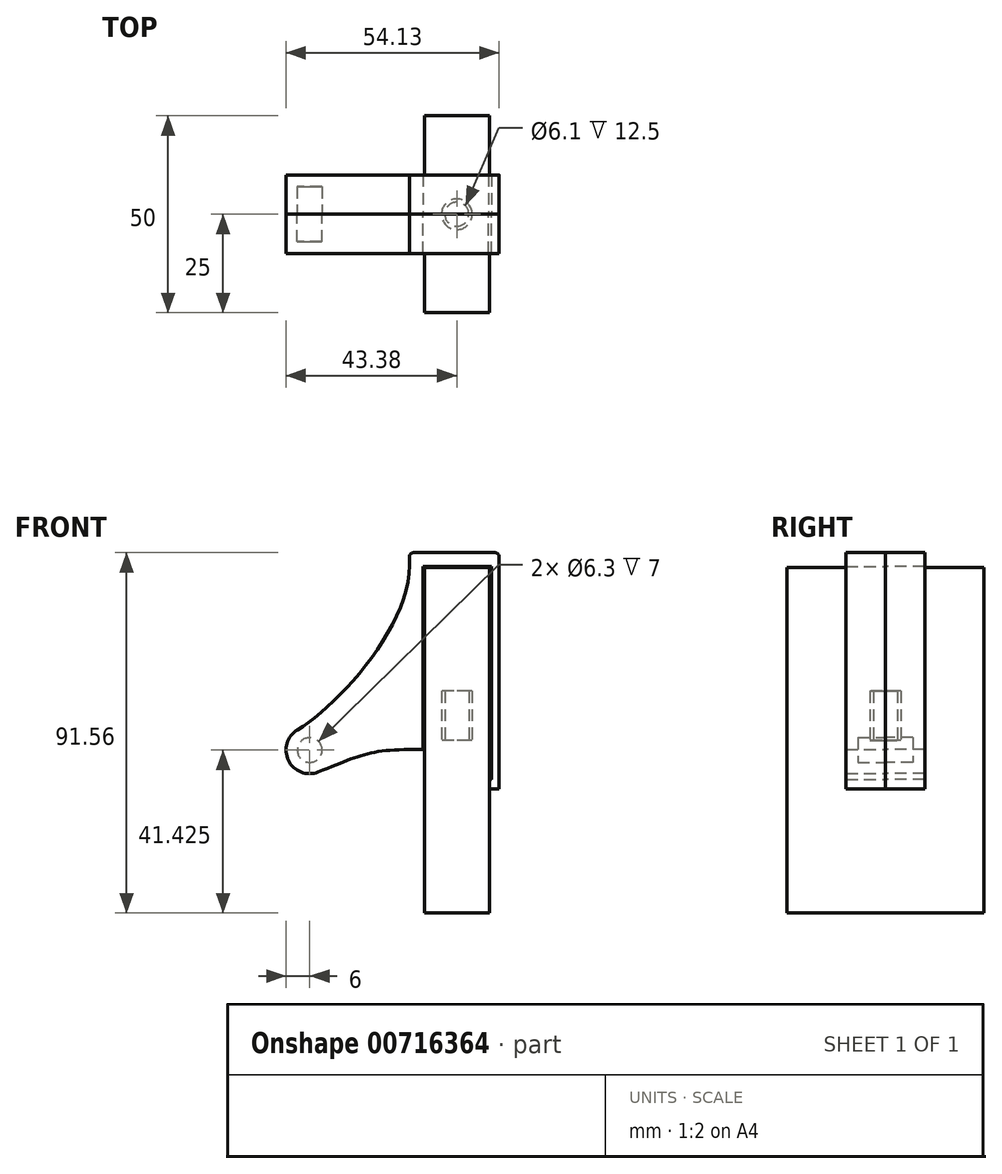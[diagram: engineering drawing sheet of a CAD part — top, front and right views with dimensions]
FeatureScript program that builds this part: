
annotation { "Feature Type Name" : "Feature", "Feature Type Description" : "" }
export const myFeature = defineFeature(function(context is Context, id is Id, definition is map)
    precondition{}
    {
        {
            var Q0;
            Q0=qCreatedBy(makeId("Front.planeOp"),FACE);
            var sketch = newSketch(context, id + "F0", { "sketchPlane" : qUnion([Q0])});
            skLineSegment(sketch, "E0.bottom", {"start": v(8.25, 43.88) * mm, "end": v(-8.25, 43.88) * mm});
            skLineSegment(sketch, "E0.top", {"start": v(8.25, -43.88) * mm, "end": v(-8.25, -43.88) * mm});
            skLineSegment(sketch, "E0.left", {"start": v(8.25, 43.88) * mm, "end": v(8.25, -43.88) * mm});
            skLineSegment(sketch, "E0.right", {"start": v(-8.25, 43.88) * mm, "end": v(-8.25, -43.88) * mm});
            skPoint(sketch, "E0.middle", {"position": v(0, 0) * mm});
            skSolve(sketch);
        }
        {
            var Q0;
            Q0 = qSketchRegion(id + "F0", true);
            extrude(context, id + "F1", {"entities" : qUnion([Q0]), "depth" : 25 * mm, "offsetDistance" : 25 * mm, "hasSecondDirection" : true, "secondDirectionOppositeDirection" : true, "secondDirectionDepth" : 25 * mm});
        }
        {
            var Q0;
            Q0=qCreatedBy(makeId("Front.planeOp"),FACE);
            var sketch = newSketch(context, id + "F2", { "sketchPlane" : qUnion([Q0])});
            skLineSegment(sketch, "E1.0", {"start": v(-8.55, 44.18) * mm, "end": v(-8.55, -25.44) * mm});
            skLineSegment(sketch, "E1.1", {"start": v(8.75, 44.18) * mm, "end": v(-8.55, 44.18) * mm});
            skLineSegment(sketch, "E1.2", {"start": v(8.75, 44.18) * mm, "end": v(8.75, -12.32) * mm});
            skLineSegment(sketch, "E2", {"start": v(8.75, -12.32) * mm, "end": v(10.75, -12.32) * mm});
            skLineSegment(sketch, "E3", {"start": v(10.75, -12.32) * mm, "end": v(10.75, 47.68) * mm});
            skLineSegment(sketch, "E4", {"start": v(10.75, 47.68) * mm, "end": v(-12.05, 47.68) * mm});
            skLineSegment(sketch, "E5", {"start": v(-12.05, 47.68) * mm, "end": v(-12.05, -2.32) * mm});
            skLineSegment(sketch, "E6", {"start": v(-12.05, -2.32) * mm, "end": v(-8.55, -2.32) * mm});
            skArc(sketch, "E7", {"start": v(8.75, -9.87) * mm, "mid": v(8.02, -11.1) * mm, "end": v(8.75, -12.32) * mm});
            skCircle(sketch, "E8", {"center": v(-37.38, -2.46) * mm, "radius": 6 * mm});
            skFitSpline(sketch, "E9", {"points": [v(-12.05, 44.4) * mm, v(-40.44, 2.7) * mm], "startDerivative": vector(0, -46.8) * mm, "endDerivative": vector(-30.7, -18.2) * mm});
            skFitSpline(sketch, "E10", {"points": [v(-12.05, -2.32) * mm, v(-35.2, -8.05) * mm], "startDerivative": vector(-32.02, 0) * mm, "endDerivative": vector(-29.24, -11.37) * mm});
            skPoint(sketch, "E11", {"position": v(-10.3, -2.32) * mm});
            skSolve(sketch);
        }
        {
            var Q0;
            Q0 = qSketchRegion(id + "F2", true);
            extrude(context, id + "F3", {"entities" : qUnion([Q0]), "depth" : 10 * mm, "offsetDistance" : 25 * mm});
        }
        {
            var Q0;
            Q0=makeQuery(id+"F3.opExtrude","CAP_FACE",FACE,{"disambiguationData":[OSD([sQuery(id+"F2.wireOp",EDGE,"E1.0"),sQuery(id+"F2.wireOp",EDGE,"E1.1"),sQuery(id+"F2.wireOp",EDGE,"E1.2"),sQuery(id+"F2.wireOp",EDGE,"E2"),sQuery(id+"F2.wireOp",EDGE,"E3"),sQuery(id+"F2.wireOp",EDGE,"E4"),sQuery(id+"F2.wireOp",EDGE,"E5"),sQuery(id+"F2.wireOp",EDGE,"E6"),sQuery(id+"F2.wireOp",EDGE,"E7"),sQuery(id+"F2.wireOp",EDGE,"e7f2464f-74c9-499f-a1c0-50080eb9df23"),sQuery(id+"F2.wireOp",EDGE,"032736fb-e714-4650-86d7-ad94455eaa23"),sQuery(id+"F2.wireOp",EDGE,"6fe076ce-718b-4dca-b48a-b1bf80613e74.filletArc")])],"isStart":true});
            var sketch = newSketch(context, id + "F4", { "sketchPlane" : qUnion([Q0])});
            skArc(sketch, "E12.0", {"start": v(40.44, 2.7) * mm, "mid": v(42.77, -5.08) * mm, "end": v(35.2, -8.05) * mm});
            skCircle(sketch, "E13", {"center": v(37.38, -2.46) * mm, "radius": 3.15 * mm});
            skSolve(sketch);
        }
        {
            var Q0;
            Q0 = qSketchRegion(id + "F4", true);
            extrude(context, id + "F5", {"entities" : qUnion([Q0]), "operationType" : NewBodyOperationType.REMOVE, "oppositeDirection" : true, "depth" : 7 * mm, "offsetDistance" : 25 * mm});
        }
        {
            var Q0;
            Q0=makeQuery(id+"F3.opExtrude","SWEPT_EDGE",EDGE,{"disambiguationData":[OSD([sQuery(id+"F2.wireOp",EDGE,"E3"),sQuery(id+"F2.wireOp",EDGE,"E4")])]});
            var Q1;
            Q1=makeQuery(id+"F3.opExtrude","SWEPT_EDGE",EDGE,{"disambiguationData":[OSD([sQuery(id+"F2.wireOp",EDGE,"E4"),sQuery(id+"F2.wireOp",EDGE,"E5")])]});
            fillet(context, id + "F6", {"entities" : qUnion([Q0, Q1]), "radius" : 1 * mm, "tangentPropagation" : true, "allowEdgeOverflow" : false});
        }
        {
            var Q0;
            Q0=makeQuery(id+"F3.opExtrude","SWEPT_BODY",BODY,{"disambiguationData":[OSD([sQuery(id+"F2.wireOp",EDGE,"E1.0"),sQuery(id+"F2.wireOp",EDGE,"E1.1"),sQuery(id+"F2.wireOp",EDGE,"E1.2"),sQuery(id+"F2.wireOp",EDGE,"E2"),sQuery(id+"F2.wireOp",EDGE,"E3"),sQuery(id+"F2.wireOp",EDGE,"E4"),sQuery(id+"F2.wireOp",EDGE,"E5"),sQuery(id+"F2.wireOp",EDGE,"E6"),sQuery(id+"F2.wireOp",EDGE,"E7"),sQuery(id+"F2.wireOp",EDGE,"e7f2464f-74c9-499f-a1c0-50080eb9df23"),sQuery(id+"F2.wireOp",EDGE,"032736fb-e714-4650-86d7-ad94455eaa23"),sQuery(id+"F2.wireOp",EDGE,"6fe076ce-718b-4dca-b48a-b1bf80613e74.filletArc")])]});
            var Q1;
            Q1=qCreatedBy(makeId("Front.planeOp"),FACE);
            mirror(context, id + "F7", {"entities" : qUnion([Q0]), "mirrorPlane" : qUnion([Q1])});
        }
        {
            var Q0;
            Q0=qCreatedBy(makeId("Top.planeOp"),FACE);
            var sketch = newSketch(context, id + "F8", { "sketchPlane" : qUnion([Q0])});
            skCircle(sketch, "E14", {"center": v(0, 0) * mm, "radius": 3.9 * mm});
            skCircle(sketch, "E15", {"center": v(0, 0) * mm, "radius": 3.05 * mm});
            skSolve(sketch);
        }
        {
            var Q0;
            Q0 = qSketchRegion(id + "F8", true);
            extrude(context, id + "F9", {"entities" : qUnion([Q0]), "depth" : 12.5 * mm, "offsetDistance" : 25 * mm});
        }
    });
